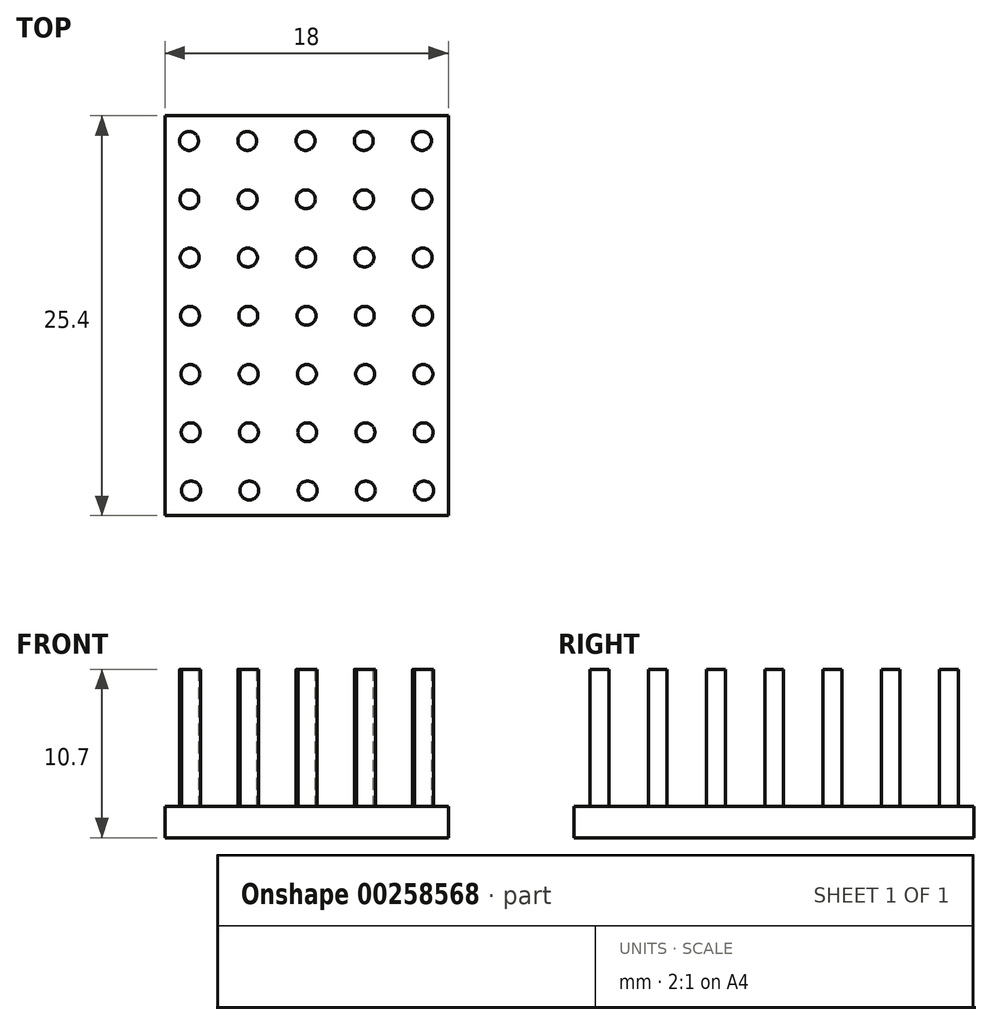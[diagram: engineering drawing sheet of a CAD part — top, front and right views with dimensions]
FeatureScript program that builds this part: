
annotation { "Feature Type Name" : "Feature", "Feature Type Description" : "" }
export const myFeature = defineFeature(function(context is Context, id is Id, definition is map)
    precondition{}
    {
        {
            var Q0;
            Q0=qCreatedBy(makeId("Top.planeOp"),FACE);
            var sketch = newSketch(context, id + "F0", { "sketchPlane" : qUnion([Q0])});
            skLineSegment(sketch, "E0.bottom", {"start": v(9, -12.7) * mm, "end": v(-9, -12.7) * mm});
            skLineSegment(sketch, "E0.top", {"start": v(9, 12.7) * mm, "end": v(-9, 12.7) * mm});
            skLineSegment(sketch, "E0.left", {"start": v(9, -12.7) * mm, "end": v(9, 12.7) * mm});
            skLineSegment(sketch, "E0.right", {"start": v(-9, -12.7) * mm, "end": v(-9, 12.7) * mm});
            skPoint(sketch, "E0.middle", {"position": v(0, 0) * mm});
            skCircle(sketch, "E1", {"center": v(-7.34, -11.1) * mm, "radius": 0.6 * mm});
            skCircle(sketch, "E2.0.1.0", {"center": v(-7.36, -7.4) * mm, "radius": 0.6 * mm});
            skCircle(sketch, "E2.0.2.0", {"center": v(-7.38, -3.7) * mm, "radius": 0.6 * mm});
            skCircle(sketch, "E2.0.3.0", {"center": v(-7.4, 0) * mm, "radius": 0.6 * mm});
            skCircle(sketch, "E2.0.4.0", {"center": v(-7.42, 3.7) * mm, "radius": 0.6 * mm});
            skCircle(sketch, "E2.0.5.0", {"center": v(-7.44, 7.4) * mm, "radius": 0.6 * mm});
            skCircle(sketch, "E2.0.6.0", {"center": v(-7.46, 11.1) * mm, "radius": 0.6 * mm});
            skCircle(sketch, "E2.1.0.0", {"center": v(-3.64, -11.1) * mm, "radius": 0.6 * mm});
            skCircle(sketch, "E2.1.1.0", {"center": v(-3.66, -7.4) * mm, "radius": 0.6 * mm});
            skCircle(sketch, "E2.1.2.0", {"center": v(-3.68, -3.7) * mm, "radius": 0.6 * mm});
            skCircle(sketch, "E2.1.3.0", {"center": v(-3.7, 0) * mm, "radius": 0.6 * mm});
            skCircle(sketch, "E2.1.4.0", {"center": v(-3.72, 3.7) * mm, "radius": 0.6 * mm});
            skCircle(sketch, "E2.1.5.0", {"center": v(-3.74, 7.4) * mm, "radius": 0.6 * mm});
            skCircle(sketch, "E2.1.6.0", {"center": v(-3.76, 11.1) * mm, "radius": 0.6 * mm});
            skCircle(sketch, "E2.2.0.0", {"center": v(0.06, -11.1) * mm, "radius": 0.6 * mm});
            skCircle(sketch, "E2.2.1.0", {"center": v(0.04, -7.4) * mm, "radius": 0.6 * mm});
            skCircle(sketch, "E2.2.2.0", {"center": v(0.02, -3.7) * mm, "radius": 0.6 * mm});
            skCircle(sketch, "E2.2.3.0", {"center": v(0, 0) * mm, "radius": 0.6 * mm});
            skCircle(sketch, "E2.2.4.0", {"center": v(-0.02, 3.7) * mm, "radius": 0.6 * mm});
            skCircle(sketch, "E2.2.5.0", {"center": v(-0.04, 7.4) * mm, "radius": 0.6 * mm});
            skCircle(sketch, "E2.2.6.0", {"center": v(-0.06, 11.1) * mm, "radius": 0.6 * mm});
            skCircle(sketch, "E2.3.0.0", {"center": v(3.76, -11.1) * mm, "radius": 0.6 * mm});
            skCircle(sketch, "E2.3.1.0", {"center": v(3.74, -7.4) * mm, "radius": 0.6 * mm});
            skCircle(sketch, "E2.3.2.0", {"center": v(3.72, -3.7) * mm, "radius": 0.6 * mm});
            skCircle(sketch, "E2.3.3.0", {"center": v(3.7, 0) * mm, "radius": 0.6 * mm});
            skCircle(sketch, "E2.3.4.0", {"center": v(3.68, 3.7) * mm, "radius": 0.6 * mm});
            skCircle(sketch, "E2.3.5.0", {"center": v(3.66, 7.4) * mm, "radius": 0.6 * mm});
            skCircle(sketch, "E2.3.6.0", {"center": v(3.64, 11.1) * mm, "radius": 0.6 * mm});
            skCircle(sketch, "E2.4.0.0", {"center": v(7.46, -11.1) * mm, "radius": 0.6 * mm});
            skCircle(sketch, "E2.4.1.0", {"center": v(7.44, -7.4) * mm, "radius": 0.6 * mm});
            skCircle(sketch, "E2.4.2.0", {"center": v(7.42, -3.7) * mm, "radius": 0.6 * mm});
            skCircle(sketch, "E2.4.3.0", {"center": v(7.4, 0) * mm, "radius": 0.6 * mm});
            skCircle(sketch, "E2.4.4.0", {"center": v(7.38, 3.7) * mm, "radius": 0.6 * mm});
            skCircle(sketch, "E2.4.5.0", {"center": v(7.36, 7.4) * mm, "radius": 0.6 * mm});
            skCircle(sketch, "E2.4.6.0", {"center": v(7.34, 11.1) * mm, "radius": 0.6 * mm});
            skLineSegment(sketch, "E2.direction1", {"start": v(-7.34, -11.1) * mm, "end": v(-3.64, -11.1) * mm, "construction": true});
            skLineSegment(sketch, "E2.direction2", {"start": v(-7.34, -11.1) * mm, "end": v(-7.36, -7.4) * mm, "construction": true});
            skSolve(sketch);
        }
        {
            var Q0;
            Q0 = qSketchRegion(id + "F0", true);
            extrude(context, id + "F1", {"entities" : qUnion([Q0]), "depth" : 2 * mm});
        }
        {
            var Q0;
            Q0=makeQuery(id+"F0.imprint","IMPRINT",FACE,{"disambiguationData":[TD([[makeQuery(id+"F0.imprint","IMPRINT",EDGE,{"derivedFrom":sQuery(id+"F0.wireOp",EDGE,"E2.3.3.0")}),1.0]])]});
            var Q1;
            Q1=makeQuery(id+"F0.imprint","IMPRINT",FACE,{"disambiguationData":[TD([[makeQuery(id+"F0.imprint","IMPRINT",EDGE,{"derivedFrom":sQuery(id+"F0.wireOp",EDGE,"E2.2.6.0")}),1.0]])]});
            var Q2;
            Q2=makeQuery(id+"F0.imprint","IMPRINT",FACE,{"disambiguationData":[TD([[makeQuery(id+"F0.imprint","IMPRINT",EDGE,{"derivedFrom":sQuery(id+"F0.wireOp",EDGE,"E2.4.1.0")}),1.0]])]});
            var Q3;
            Q3=makeQuery(id+"F0.imprint","IMPRINT",FACE,{"disambiguationData":[TD([[makeQuery(id+"F0.imprint","IMPRINT",EDGE,{"derivedFrom":sQuery(id+"F0.wireOp",EDGE,"E2.0.1.0")}),1.0]])]});
            var Q4;
            Q4=makeQuery(id+"F0.imprint","IMPRINT",FACE,{"disambiguationData":[TD([[makeQuery(id+"F0.imprint","IMPRINT",EDGE,{"derivedFrom":sQuery(id+"F0.wireOp",EDGE,"E2.1.1.0")}),1.0]])]});
            var Q5;
            Q5=makeQuery(id+"F0.imprint","IMPRINT",FACE,{"disambiguationData":[TD([[makeQuery(id+"F0.imprint","IMPRINT",EDGE,{"derivedFrom":sQuery(id+"F0.wireOp",EDGE,"E2.4.0.0")}),1.0]])]});
            var Q6;
            Q6=makeQuery(id+"F0.imprint","IMPRINT",FACE,{"disambiguationData":[TD([[makeQuery(id+"F0.imprint","IMPRINT",EDGE,{"derivedFrom":sQuery(id+"F0.wireOp",EDGE,"E2.0.5.0")}),1.0]])]});
            var Q7;
            Q7=makeQuery(id+"F0.imprint","IMPRINT",FACE,{"disambiguationData":[TD([[makeQuery(id+"F0.imprint","IMPRINT",EDGE,{"derivedFrom":sQuery(id+"F0.wireOp",EDGE,"E2.4.6.0")}),1.0]])]});
            var Q8;
            Q8=makeQuery(id+"F0.imprint","IMPRINT",FACE,{"disambiguationData":[TD([[makeQuery(id+"F0.imprint","IMPRINT",EDGE,{"derivedFrom":sQuery(id+"F0.wireOp",EDGE,"E2.2.0.0")}),1.0]])]});
            var Q9;
            Q9=makeQuery(id+"F0.imprint","IMPRINT",FACE,{"disambiguationData":[TD([[makeQuery(id+"F0.imprint","IMPRINT",EDGE,{"derivedFrom":sQuery(id+"F0.wireOp",EDGE,"E2.1.6.0")}),1.0]])]});
            var Q10;
            Q10=makeQuery(id+"F0.imprint","IMPRINT",FACE,{"disambiguationData":[TD([[makeQuery(id+"F0.imprint","IMPRINT",EDGE,{"derivedFrom":sQuery(id+"F0.wireOp",EDGE,"E2.1.0.0")}),1.0]])]});
            var Q11;
            Q11=makeQuery(id+"F0.imprint","IMPRINT",FACE,{"disambiguationData":[TD([[makeQuery(id+"F0.imprint","IMPRINT",EDGE,{"derivedFrom":sQuery(id+"F0.wireOp",EDGE,"E2.3.6.0")}),1.0]])]});
            var Q12;
            Q12=makeQuery(id+"F0.imprint","IMPRINT",FACE,{"disambiguationData":[TD([[makeQuery(id+"F0.imprint","IMPRINT",EDGE,{"derivedFrom":sQuery(id+"F0.wireOp",EDGE,"E2.2.3.0")}),1.0]])]});
            var Q13;
            Q13=makeQuery(id+"F0.imprint","IMPRINT",FACE,{"disambiguationData":[TD([[makeQuery(id+"F0.imprint","IMPRINT",EDGE,{"derivedFrom":sQuery(id+"F0.wireOp",EDGE,"E2.2.1.0")}),1.0]])]});
            var Q14;
            Q14=makeQuery(id+"F0.imprint","IMPRINT",FACE,{"disambiguationData":[TD([[makeQuery(id+"F0.imprint","IMPRINT",EDGE,{"derivedFrom":sQuery(id+"F0.wireOp",EDGE,"E2.4.5.0")}),1.0]])]});
            var Q15;
            Q15=makeQuery(id+"F0.imprint","IMPRINT",FACE,{"disambiguationData":[TD([[makeQuery(id+"F0.imprint","IMPRINT",EDGE,{"derivedFrom":sQuery(id+"F0.wireOp",EDGE,"E2.1.2.0")}),1.0]])]});
            var Q16;
            Q16=makeQuery(id+"F0.imprint","IMPRINT",FACE,{"disambiguationData":[TD([[makeQuery(id+"F0.imprint","IMPRINT",EDGE,{"derivedFrom":sQuery(id+"F0.wireOp",EDGE,"E2.4.2.0")}),1.0]])]});
            var Q17;
            Q17=makeQuery(id+"F0.imprint","IMPRINT",FACE,{"disambiguationData":[TD([[makeQuery(id+"F0.imprint","IMPRINT",EDGE,{"derivedFrom":sQuery(id+"F0.wireOp",EDGE,"E2.4.4.0")}),1.0]])]});
            var Q18;
            Q18=makeQuery(id+"F0.imprint","IMPRINT",FACE,{"disambiguationData":[TD([[makeQuery(id+"F0.imprint","IMPRINT",EDGE,{"derivedFrom":sQuery(id+"F0.wireOp",EDGE,"E2.0.3.0")}),1.0]])]});
            var Q19;
            Q19=makeQuery(id+"F0.imprint","IMPRINT",FACE,{"disambiguationData":[TD([[makeQuery(id+"F0.imprint","IMPRINT",EDGE,{"derivedFrom":sQuery(id+"F0.wireOp",EDGE,"E2.0.4.0")}),1.0]])]});
            var Q20;
            Q20=makeQuery(id+"F0.imprint","IMPRINT",FACE,{"disambiguationData":[TD([[makeQuery(id+"F0.imprint","IMPRINT",EDGE,{"derivedFrom":sQuery(id+"F0.wireOp",EDGE,"E2.3.1.0")}),1.0]])]});
            var Q21;
            Q21=makeQuery(id+"F0.imprint","IMPRINT",FACE,{"disambiguationData":[TD([[makeQuery(id+"F0.imprint","IMPRINT",EDGE,{"derivedFrom":sQuery(id+"F0.wireOp",EDGE,"E2.2.2.0")}),1.0]])]});
            var Q22;
            Q22=makeQuery(id+"F0.imprint","IMPRINT",FACE,{"disambiguationData":[TD([[makeQuery(id+"F0.imprint","IMPRINT",EDGE,{"derivedFrom":sQuery(id+"F0.wireOp",EDGE,"E2.2.4.0")}),1.0]])]});
            var Q23;
            Q23=makeQuery(id+"F0.imprint","IMPRINT",FACE,{"disambiguationData":[TD([[makeQuery(id+"F0.imprint","IMPRINT",EDGE,{"derivedFrom":sQuery(id+"F0.wireOp",EDGE,"E2.1.4.0")}),1.0]])]});
            var Q24;
            Q24=makeQuery(id+"F0.imprint","IMPRINT",FACE,{"disambiguationData":[TD([[makeQuery(id+"F0.imprint","IMPRINT",EDGE,{"derivedFrom":sQuery(id+"F0.wireOp",EDGE,"E2.3.2.0")}),1.0]])]});
            var Q25;
            Q25=makeQuery(id+"F0.imprint","IMPRINT",FACE,{"disambiguationData":[TD([[makeQuery(id+"F0.imprint","IMPRINT",EDGE,{"derivedFrom":sQuery(id+"F0.wireOp",EDGE,"E2.3.4.0")}),1.0]])]});
            var Q26;
            Q26=makeQuery(id+"F0.imprint","IMPRINT",FACE,{"disambiguationData":[TD([[makeQuery(id+"F0.imprint","IMPRINT",EDGE,{"derivedFrom":sQuery(id+"F0.wireOp",EDGE,"E2.4.3.0")}),1.0]])]});
            var Q27;
            Q27=makeQuery(id+"F0.imprint","IMPRINT",FACE,{"disambiguationData":[TD([[makeQuery(id+"F0.imprint","IMPRINT",EDGE,{"derivedFrom":sQuery(id+"F0.wireOp",EDGE,"E2.0.2.0")}),1.0]])]});
            var Q28;
            Q28=makeQuery(id+"F0.imprint","IMPRINT",FACE,{"disambiguationData":[TD([[makeQuery(id+"F0.imprint","IMPRINT",EDGE,{"derivedFrom":sQuery(id+"F0.wireOp",EDGE,"E2.2.5.0")}),1.0]])]});
            var Q29;
            Q29=makeQuery(id+"F0.imprint","IMPRINT",FACE,{"disambiguationData":[TD([[makeQuery(id+"F0.imprint","IMPRINT",EDGE,{"derivedFrom":sQuery(id+"F0.wireOp",EDGE,"E2.0.6.0")}),1.0]])]});
            var Q30;
            Q30=makeQuery(id+"F0.imprint","IMPRINT",FACE,{"disambiguationData":[TD([[makeQuery(id+"F0.imprint","IMPRINT",EDGE,{"derivedFrom":sQuery(id+"F0.wireOp",EDGE,"E2.3.5.0")}),1.0]])]});
            var Q31;
            Q31=makeQuery(id+"F0.imprint","IMPRINT",FACE,{"disambiguationData":[TD([[makeQuery(id+"F0.imprint","IMPRINT",EDGE,{"derivedFrom":sQuery(id+"F0.wireOp",EDGE,"E1")}),1.0]])]});
            var Q32;
            Q32=makeQuery(id+"F0.imprint","IMPRINT",FACE,{"disambiguationData":[TD([[makeQuery(id+"F0.imprint","IMPRINT",EDGE,{"derivedFrom":sQuery(id+"F0.wireOp",EDGE,"E2.1.3.0")}),1.0]])]});
            var Q33;
            Q33=makeQuery(id+"F0.imprint","IMPRINT",FACE,{"disambiguationData":[TD([[makeQuery(id+"F0.imprint","IMPRINT",EDGE,{"derivedFrom":sQuery(id+"F0.wireOp",EDGE,"E2.1.5.0")}),1.0]])]});
            var Q34;
            Q34=makeQuery(id+"F0.imprint","IMPRINT",FACE,{"disambiguationData":[TD([[makeQuery(id+"F0.imprint","IMPRINT",EDGE,{"derivedFrom":sQuery(id+"F0.wireOp",EDGE,"E2.3.0.0")}),1.0]])]});
            extrude(context, id + "F2", {"entities" : qUnion([Q0, Q1, Q2, Q3, Q4, Q5, Q6, Q7, Q8, Q9, Q10, Q11, Q12, Q13, Q14, Q15, Q16, Q17, Q18, Q19, Q20, Q21, Q22, Q23, Q24, Q25, Q26, Q27, Q28, Q29, Q30, Q31, Q32, Q33, Q34]), "operationType" : NewBodyOperationType.ADD, "depth" : 10.7 * mm});
        }
    });
